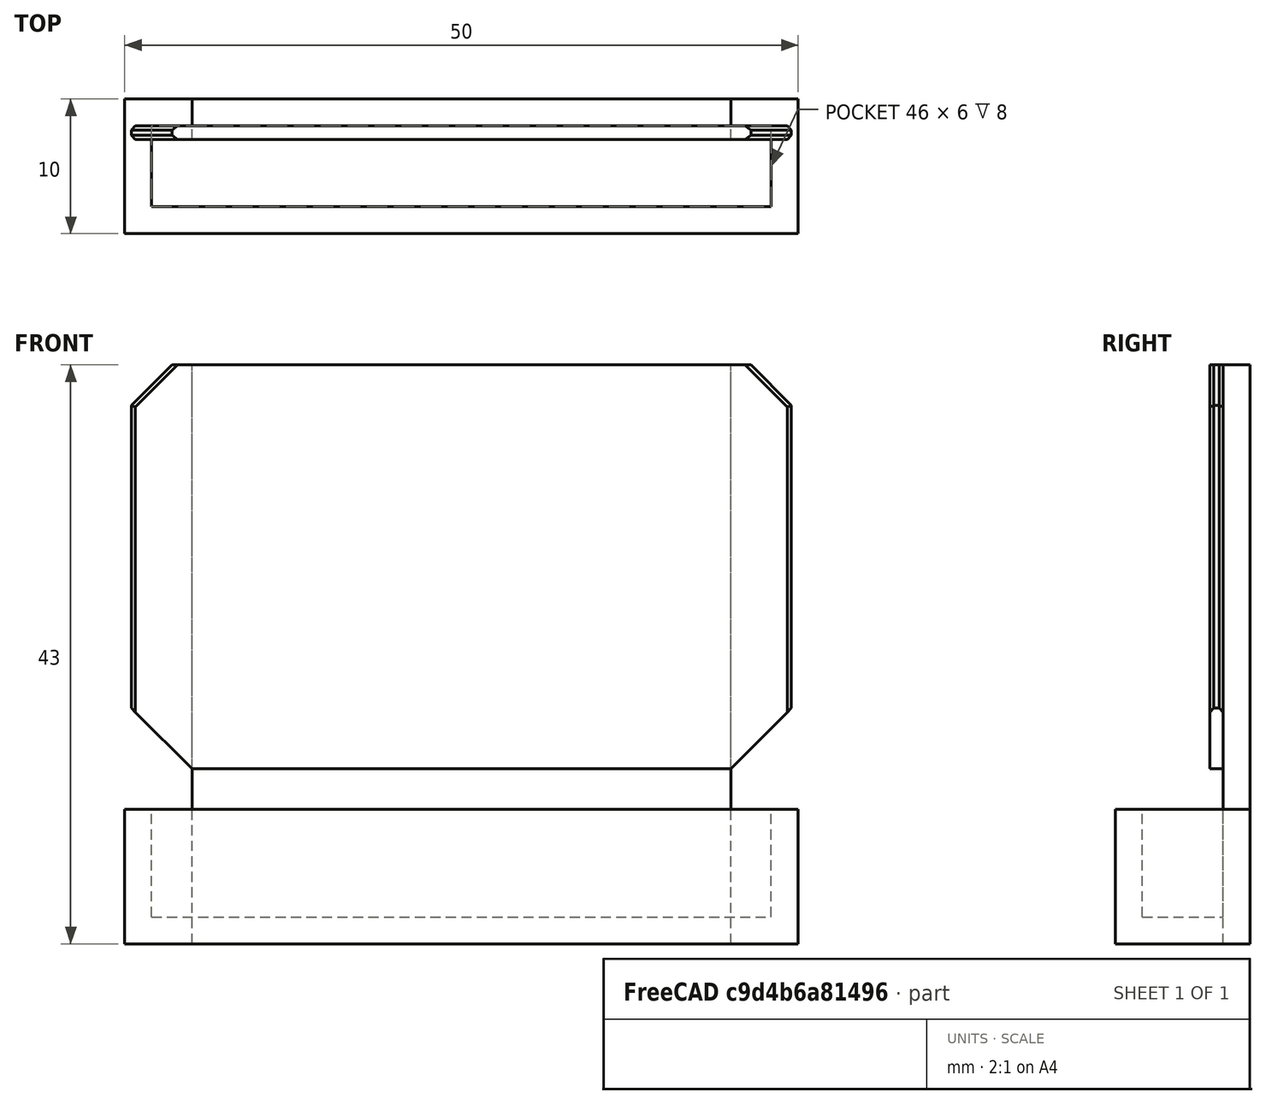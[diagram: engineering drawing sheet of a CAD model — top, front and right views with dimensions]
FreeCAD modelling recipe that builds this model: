
FCSTD DOCUMENT  (FreeCAD 0.15R4671 (Git))
Label: Phone_Stand_Holder
License: All rights reserved
LicenseURL: http://en.wikipedia.org/wiki/All_rights_reserved
objects: Part::Box×4, Part::Chamfer×4, Part::Cut×1
note: 9 computed .brp shape members not serialized (recipe doc carries the construction recipe); baked Part::Feature solids carry a one-line shape summary decoded from their .brp

FEATURE [Part::Box] Box  label="Cube"
  Height = 10
  Length = 50
  Width = 10
FEATURE [Part::Box] Box044  label="Cube039"
  Height = 43
  Length = 40
  Placement = pos=(5,8,0) rot=(0,0,1;0rad)
  Width = 2
FEATURE [Part::Box] Box045  label="Cube040"
  Height = 8
  Length = 46
  Placement = pos=(2,2,2) rot=(0,0,1;0rad)
  Width = 6
FEATURE [Part::Cut] Cut
  Base = -> Box
  Tool = -> Box045
FEATURE [Part::Box] Box046  label="Cube041"
  Height = 30
  Length = 49
  Placement = pos=(0.5,6,12) rot=(0,0,1;0rad)
  Width = 1
FEATURE [Part::Chamfer] Chamfer
  Base = -> Box046
  Edges = 2 edges r=4.5: [Edge4,Edge8]
  Placement = pos=(0,1,1) rot=(0,0,1;0rad)
FEATURE [Part::Chamfer] Chamfer001
  Base = -> Chamfer
  Edges = 2 edges r=3: [Edge3,Edge13]
FEATURE [Part::Chamfer] Chamfer002
  Base = -> Chamfer001
  Edges = 4 edges r=0.3: [Edge1,Edge4,Edge11,Edge20]
FEATURE [Part::Chamfer] Chamfer003
  Base = -> Chamfer002
  Edges = 4 edges r=0.3: [Edge5,Edge8,Edge18,Edge24]
